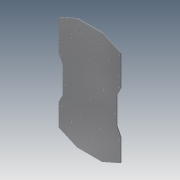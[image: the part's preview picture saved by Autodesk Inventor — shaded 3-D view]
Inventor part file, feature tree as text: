
AUTODESK INVENTOR PART (.ipt)
format: ipt  version: 2015 (Build 190159000, 159)  size: 153,088 bytes
history: native  units: mm
features: extrude x1, sketch x1
ambient origin geometry x8: Origin, YZ Plane, XZ Plane, XY Plane, X Axis, Y Axis, Z Axis, Center Point
bodies: Solid1 (feature_tree)
feature tree (2):
  extrude  "Extrusion1"  Depth=2.0mm
  sketch  "Sketch1"  dims[d0=4.0mm d1=4.0mm d2=4.0mm d3=4.0mm d4=4.0mm d5=4.0mm d6=4.0mm d7=4.0mm d8=4.0mm d9=4.0mm d10=4.0mm d11=4.0mm d12=4.0mm d13=4.0mm d14=4.0mm d15=4.0mm d16=4.0mm d17=4.0mm d18=4.0mm d19=4.0mm d20=4.0mm d21=4.0mm d22=4.0mm d23=4.0mm d24=4.0mm d25=2.0mm d26=0.0mm]
